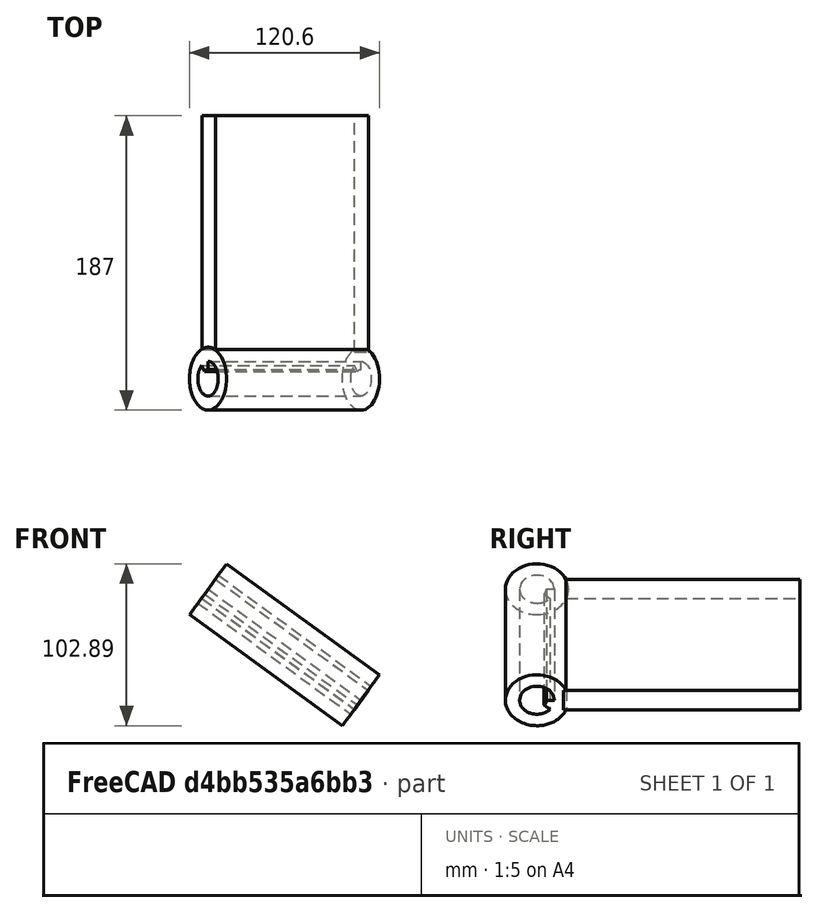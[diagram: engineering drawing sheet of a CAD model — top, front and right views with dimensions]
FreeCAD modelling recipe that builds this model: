
FCSTD DOCUMENT  (FreeCAD 0.16R6704 (Git))
Label: Plataforma izquierda
License: All rights reserved
LicenseURL: http://en.wikipedia.org/wiki/All_rights_reserved
objects: Part::Cylinder×6, Part::Cut×4, Part::MultiFuse×2, Part::Box×1
note: 13 computed .brp shape members not serialized (recipe doc carries the construction recipe); baked Part::Feature solids carry a one-line shape summary decoded from their .brp

FEATURE [Part::Box] Box130  label="Cubo093"
  Height = 15
  Length = 120
  Placement = pos=(-296,17,92.9) rot=(0,1,0;0.628319rad)
  Width = 150
FEATURE [Part::Cylinder] Cylinder278  label="Cilindro165"
  Angle = 360
  Height = 120
  Placement = pos=(-292,0,98.9) rot=(0,1,0;2.19911rad)
  Radius = 20
FEATURE [Part::Cylinder] Cylinder279  label="Cilindro166"
  Angle = 360
  Height = 120
  Placement = pos=(-292,0,98.9) rot=(0,1,0;2.19911rad)
  Radius = 11
FEATURE [Part::Cut] Cut297
  Base = -> Cylinder278
  Tool = -> Cylinder279
FEATURE [Part::Cylinder] Cylinder280  label="Cilindro167"
  Angle = 50
  Height = 120
  Placement = pos=(-292,0,98.9) rot=(0,1,0;2.19911rad)
  Radius = 11
FEATURE [Part::Cylinder] Cylinder281  label="Cilindro168"
  Angle = 360
  Height = 130
  Placement = pos=(-292,0,98.9) rot=(0,1,0;2.19911rad)
  Radius = 5
FEATURE [Part::Cut] Cut298
  Base = -> Cylinder280
  Tool = -> Cylinder281
FEATURE [Part::Cylinder] Cylinder282  label="Cilindro169"
  Angle = 90
  Height = 120
  Placement = pos=(-292,0,98.9) rot=(0,1,0;2.19911rad)
  Radius = 11
FEATURE [Part::Cylinder] Cylinder283  label="Cilindro170"
  Angle = 360
  Height = 130
  Placement = pos=(-292,0,98.9) rot=(0,1,0;2.19911rad)
  Radius = 6
FEATURE [Part::Cut] Cut299
  Base = -> Cylinder282
  Tool = -> Cylinder283
FEATURE [Part::Cut] Cut300
  Base = -> Cut299
  Tool = -> Cut298
FEATURE [Part::MultiFuse] Fusion078  label="Fusion081"
  Shapes = -> [Cut297,Cut300]
FEATURE [Part::MultiFuse] Fusion079
  Placement = pos=(-524,0,-105) rot=(0,0,1;0rad)
  Shapes = -> [Fusion078,Box130]
